# Revit family: Manifold_NPT-JCI_Sapphire_Plus-(70bar)Novec1230
name_source: partatom
category: Specialty Equipment
revit_build: Autodesk Revit 2017 (Build: 20171027_0315(x64)
units: mm (PartAtom-declared; Revit-internal decimal feet)

## family parameters
Always vertical = No
Cut with Voids When Loaded = No
OmniClass Number = 23.29.33.13.11
Part Type = Normal
Room Calculation Point = No
Round Connector Dimension = Use Diameter
Shared = No
Work Plane-Based = Yes

## types (10) — shared parameters
Assembly Code = D4090300
Date Modified = YYYY/MM/DD
Equipment Abbreviation = MP
Family Version = 1.0
Fire Suppression Agent = ''3M Novec'' 1230 Fire Protection Fluid
Manufacturer = Johnson Controls, Inc.
Model Disclaimer = For More Information Contact JOHNSON CONTROLS
Operating Temperature = 122 °F
Product Documentation Link = http://www.sapphireplus.com
Product Material = JCI - Metal - Stainless Steel - Satin
Product Page URL = http://www.sapphireplus.com
Unit Assembly = Sapphire Plus_Manifold
zero-valued in all types: Default Elevation

## per-type parameters (varying)
| type | Description | Length | Model | NPT Type | Nominal Type | Number of Inlets | Part Number | Pipe Diameter | URL |
| 80mm_NPT_2PT | 80mm_NPT_2PT | 800 mm  [stored 2.62467 ft] | 307700004 | 2 | 80 | 2 | 307700004 | 80 mm  [stored 0.262467 ft] | http://www.sapphireplus.com |
| 80mm_NPT_3PT | 80mm_NPT_3PT | 1300 mm  [stored 4.26509 ft] | 307700005 | 3 | 80 | 3 | 307700005 | 80 mm  [stored 0.262467 ft] | http://www.sapphireplus.com |
| 80mm_NPT_4PT | 80mm_NPT_4PT | 1800 mm  [stored 5.90551 ft] | 307700006 | 4 | 80 | 4 | 307700006 | 80 mm  [stored 0.262467 ft] | http://www.sapphireplus.com |
| 80mm_NPT_5PT | 80mm_NPT_5PT | 2300 mm  [stored 7.54593 ft] | 307700007 | 5 | 80 | 5 | 307700007 | 80 mm  [stored 0.262467 ft] | http://www.sapphireplus.com |
| 80mm_NPT_6PT | 80mm_NPT_6PT | 2800 mm  [stored 9.18635 ft] | 307700008 | 6 | 80 | 6 | 307700008 | 80 mm  [stored 0.262467 ft] | http://www.sapphireplus.com |
| 100mm_NPT_2PT | 100 mm Manifold NPT – 2 PT | 800 mm  [stored 2.62467 ft] | 307700009 | 2 | 100 | 2 | 307700009 | 100 mm  [stored 0.328084 ft] | https://www.ansul.com |
| 100mm_NPT_4PT | 100mm_NPT_4PT | 1800 mm  [stored 5.90551 ft] | 307700011 | 4 | 100 | 4 | 307700011 | 100 mm  [stored 0.328084 ft] | http://www.sapphireplus.com |
| 100mm_NPT_5PT | 100mm_NPT_5PT | 2300 mm  [stored 7.54593 ft] | 307700012 | 5 | 100 | 5 | 307700012 | 100 mm  [stored 0.328084 ft] | http://www.sapphireplus.com |
| 100mm_NPT_6PT | 100mm_NPT_6PT | 2800 mm  [stored 9.18635 ft] | 307700013 | 6 | 100 | 6 | 307700013 | 100 mm  [stored 0.328084 ft] | http://www.sapphireplus.com |
| 100mm_NPT_3PT | 100mm_NPT_3PT | 1300 mm  [stored 4.26509 ft] | 307700010 | 3 | 100 | 3 | 307700010 | 100 mm  [stored 0.328084 ft] | http://www.sapphireplus.com |

note: [stored X ft] marks values corroborated as IEEE doubles in the binary element streams (Revit-internal decimal feet)

## geometry (parser evidence)
native form markers: Sweep x1
no freeform markers — native parametric forms only
